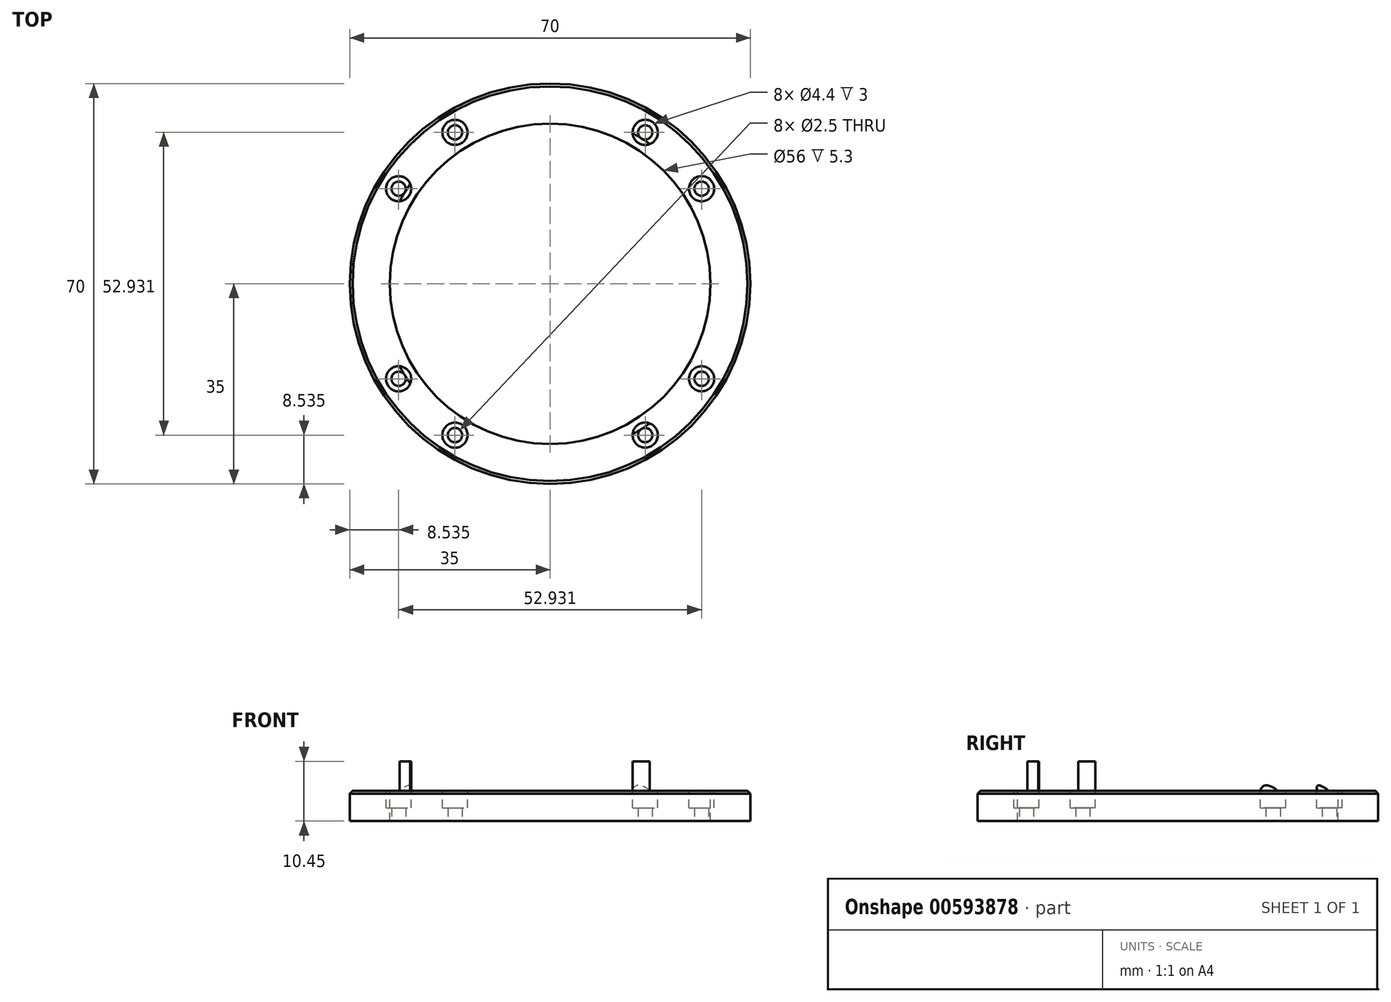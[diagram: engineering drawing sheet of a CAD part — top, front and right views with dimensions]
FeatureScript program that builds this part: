
annotation { "Feature Type Name" : "Feature", "Feature Type Description" : "" }
export const myFeature = defineFeature(function(context is Context, id is Id, definition is map)
    precondition{}
    {
        {
            var Q0;
            Q0=qCreatedBy(makeId("Top.planeOp"),FACE);
            var sketch = newSketch(context, id + "F0", { "sketchPlane" : qUnion([Q0])});
            skCircle(sketch, "E0", {"center": v(0, 0) * mm, "radius": 27 * mm});
            skCircle(sketch, "E1", {"center": v(0, 0) * mm, "radius": 25 * mm});
            skCircle(sketch, "E2", {"center": v(0, 0) * mm, "radius": 34.5 * mm});
            skLineSegment(sketch, "E3", {"start": v(-12.5, 31.4) * mm, "end": v(-12.5, 32.16) * mm});
            skLineSegment(sketch, "E4", {"start": v(-12.5, 32.16) * mm, "end": v(-12.5, 23.93) * mm});
            skLineSegment(sketch, "E5", {"start": v(12.5, 31.4) * mm, "end": v(12.5, 32.16) * mm});
            skLineSegment(sketch, "E6", {"start": v(12.5, 32.16) * mm, "end": v(12.5, 23.93) * mm});
            skLineSegment(sketch, "E7.1.0", {"start": v(-32.16, -12.5) * mm, "end": v(-23.93, -12.5) * mm});
            skLineSegment(sketch, "E7.1.1", {"start": v(-32.16, 12.5) * mm, "end": v(-23.93, 12.5) * mm});
            skLineSegment(sketch, "E7.2.0", {"start": v(12.5, -32.16) * mm, "end": v(12.5, -23.93) * mm});
            skLineSegment(sketch, "E7.2.1", {"start": v(-12.5, -32.16) * mm, "end": v(-12.5, -23.93) * mm});
            skLineSegment(sketch, "E7.3.0", {"start": v(32.16, 12.5) * mm, "end": v(23.93, 12.5) * mm});
            skLineSegment(sketch, "E7.3.1", {"start": v(32.16, -12.5) * mm, "end": v(23.93, -12.5) * mm});
            skCircle(sketch, "E8", {"center": v(0, 0) * mm, "radius": 28.99 * mm});
            skLineSegment(sketch, "E9", {"start": v(12.5, 32.16) * mm, "end": v(12.5, 26.16) * mm});
            skLineSegment(sketch, "E10", {"start": v(-12.5, 32.16) * mm, "end": v(-12.5, 26.16) * mm});
            skLineSegment(sketch, "E11", {"start": v(0, 34.5) * mm, "end": v(0, 30.5) * mm});
            skLineSegment(sketch, "E12", {"start": v(0, 30.5) * mm, "end": v(0, 32) * mm});
            skCircle(sketch, "E13", {"center": v(0, 32) * mm, "radius": 1.5 * mm});
            skLineSegment(sketch, "E14", {"start": v(-1.5, 32) * mm, "end": v(-1.5, 34.47) * mm});
            skLineSegment(sketch, "E15", {"start": v(1.5, 32) * mm, "end": v(1.5, 34.47) * mm});
            skCircle(sketch, "E16.1.0", {"center": v(-32, 0) * mm, "radius": 1.5 * mm});
            skLineSegment(sketch, "E16.1.1", {"start": v(-34.5, 0) * mm, "end": v(-30.5, 0) * mm});
            skLineSegment(sketch, "E16.1.2", {"start": v(-32, -1.5) * mm, "end": v(-34.47, -1.5) * mm});
            skLineSegment(sketch, "E16.1.3", {"start": v(-32, 1.5) * mm, "end": v(-34.47, 1.5) * mm});
            skCircle(sketch, "E16.2.0", {"center": v(0, -32) * mm, "radius": 1.5 * mm});
            skLineSegment(sketch, "E16.2.1", {"start": v(0, -34.5) * mm, "end": v(0, -30.5) * mm});
            skLineSegment(sketch, "E16.2.2", {"start": v(1.5, -32) * mm, "end": v(1.5, -34.47) * mm});
            skLineSegment(sketch, "E16.2.3", {"start": v(-1.5, -32) * mm, "end": v(-1.5, -34.47) * mm});
            skCircle(sketch, "E16.3.0", {"center": v(32, 0) * mm, "radius": 1.5 * mm});
            skLineSegment(sketch, "E16.3.1", {"start": v(34.5, 0) * mm, "end": v(30.5, 0) * mm});
            skLineSegment(sketch, "E16.3.2", {"start": v(32, 1.5) * mm, "end": v(34.47, 1.5) * mm});
            skLineSegment(sketch, "E16.3.3", {"start": v(32, -1.5) * mm, "end": v(34.47, -1.5) * mm});
            skSolve(sketch);
        }
        {
            var Q0;
            {var subQ0=sQuery(id+"F0.wireOp",EDGE,"E7.1.0");Q0=makeQuery(id+"F0.imprint","IMPRINT",FACE,{"disambiguationData":[TD([[makeQuery(id+"F0.imprint","IMPRINT",EDGE,{"derivedFrom":subQ0}),1.0]])]});}
            var Q1;
            {var subQ0=sQuery(id+"F0.wireOp",EDGE,"E7.2.0");Q1=makeQuery(id+"F0.imprint","IMPRINT",FACE,{"disambiguationData":[TD([[makeQuery(id+"F0.imprint","IMPRINT",EDGE,{"derivedFrom":subQ0}),1.0]])]});}
            var Q2;
            {var subQ0=sQuery(id+"F0.wireOp",EDGE,"E7.3.0");Q2=makeQuery(id+"F0.imprint","IMPRINT",FACE,{"disambiguationData":[TD([[makeQuery(id+"F0.imprint","IMPRINT",EDGE,{"derivedFrom":subQ0}),1.0]])]});}
            var Q3;
            {var subQ0=sQuery(id+"F0.wireOp",EDGE,"E4");var subQ3=makeQuery(id+"F0.imprint","IMPRINT",VERTEX,{"derivedFrom":subQ0});Q3=makeQuery(id+"F0.imprint","IMPRINT",FACE,{"disambiguationData":[TD([[makeQuery(id+"F0.imprint","IMPRINT",EDGE,{"disambiguationData":[TD([[subQ3,1.0]])],"derivedFrom":subQ0}),1.0]])]});}
            var Q4;
            {var subQ0=sQuery(id+"F0.wireOp",EDGE,"E4");var subQ1=sQuery(id+"F0.wireOp",EDGE,"E0");var subQ2=makeQuery(id+"F0.imprint","INTERSECT",VERTEX,{"derivedFrom":[subQ1,subQ0]});Q4=makeQuery(id+"F0.imprint","IMPRINT",FACE,{"disambiguationData":[TD([[makeQuery(id+"F0.imprint","IMPRINT",EDGE,{"disambiguationData":[TD([[subQ2,-1.0]])],"derivedFrom":subQ1}),-1.0]])]});}
            var Q5;
            {var subQ0=sQuery(id+"F0.wireOp",EDGE,"E6");var subQ1=sQuery(id+"F0.wireOp",EDGE,"E0");var subQ2=makeQuery(id+"F0.imprint","INTERSECT",VERTEX,{"derivedFrom":[subQ1,subQ0]});Q5=makeQuery(id+"F0.imprint","IMPRINT",FACE,{"disambiguationData":[TD([[makeQuery(id+"F0.imprint","IMPRINT",EDGE,{"disambiguationData":[TD([[subQ2,1.0]])],"derivedFrom":subQ1}),-1.0]])]});}
            var Q6;
            {var subQ0=sQuery(id+"F0.wireOp",EDGE,"E7.2.0");var subQ1=sQuery(id+"F0.wireOp",EDGE,"E0");var subQ2=makeQuery(id+"F0.imprint","INTERSECT",VERTEX,{"derivedFrom":[subQ1,subQ0]});Q6=makeQuery(id+"F0.imprint","IMPRINT",FACE,{"disambiguationData":[TD([[makeQuery(id+"F0.imprint","IMPRINT",EDGE,{"disambiguationData":[TD([[subQ2,-1.0]])],"derivedFrom":subQ1}),-1.0]])]});}
            var Q7;
            {var subQ0=sQuery(id+"F0.wireOp",EDGE,"E7.1.0");var subQ1=sQuery(id+"F0.wireOp",EDGE,"E0");var subQ2=makeQuery(id+"F0.imprint","INTERSECT",VERTEX,{"derivedFrom":[subQ1,subQ0]});Q7=makeQuery(id+"F0.imprint","IMPRINT",FACE,{"disambiguationData":[TD([[makeQuery(id+"F0.imprint","IMPRINT",EDGE,{"disambiguationData":[TD([[subQ2,-1.0]])],"derivedFrom":subQ1}),-1.0]])]});}
            var Q8;
            {var subQ0=sQuery(id+"F0.wireOp",EDGE,"E4");var subQ1=sQuery(id+"F0.wireOp",EDGE,"E0");var subQ2=makeQuery(id+"F0.imprint","INTERSECT",VERTEX,{"derivedFrom":[subQ1,subQ0]});Q8=makeQuery(id+"F0.imprint","IMPRINT",FACE,{"disambiguationData":[TD([[makeQuery(id+"F0.imprint","IMPRINT",EDGE,{"disambiguationData":[TD([[subQ2,1.0]])],"derivedFrom":subQ1}),-1.0]])]});}
            var Q9;
            {var subQ0=sQuery(id+"F0.wireOp",EDGE,"E9");var subQ3=makeQuery(id+"F0.imprint","IMPRINT",VERTEX,{"derivedFrom":subQ0});Q9=makeQuery(id+"F0.imprint","IMPRINT",FACE,{"disambiguationData":[TD([[makeQuery(id+"F0.imprint","IMPRINT",EDGE,{"disambiguationData":[TD([[subQ3,1.0]])],"derivedFrom":subQ0}),-1.0]])]});}
            var Q10;
            {var subQ11=sQuery(id+"F0.wireOp",EDGE,"E16.3.2");Q10=makeQuery(id+"F0.imprint","IMPRINT",FACE,{"disambiguationData":[TD([[makeQuery(id+"F0.imprint","IMPRINT",EDGE,{"derivedFrom":subQ11}),1.0]])]});}
            var Q11;
            {var subQ6=sQuery(id+"F0.wireOp",EDGE,"E16.2.2");Q11=makeQuery(id+"F0.imprint","IMPRINT",FACE,{"disambiguationData":[TD([[makeQuery(id+"F0.imprint","IMPRINT",EDGE,{"derivedFrom":subQ6}),1.0]])]});}
            var Q12;
            {var subQ7=sQuery(id+"F0.wireOp",EDGE,"E16.1.2");Q12=makeQuery(id+"F0.imprint","IMPRINT",FACE,{"disambiguationData":[TD([[makeQuery(id+"F0.imprint","IMPRINT",EDGE,{"derivedFrom":subQ7}),1.0]])]});}
            extrude(context, id + "F1", {"entities" : qUnion([Q0, Q1, Q2, Q3, Q4, Q5, Q6, Q7, Q8, Q9, Q10, Q11, Q12]), "depth" : 2 * mm, "offsetDistance" : 25 * mm});
        }
        {
            var Q0;
            Q0=qCreatedBy(makeId("Top.planeOp"),FACE);
            var sketch = newSketch(context, id + "F2", { "sketchPlane" : qUnion([Q0])});
            skCircle(sketch, "E17", {"center": v(0, 0) * mm, "radius": 27.1 * mm});
            skCircle(sketch, "E18", {"center": v(0, 0) * mm, "radius": 24.55 * mm});
            skSolve(sketch);
        }
        {
            var Q0;
            Q0=makeQuery(id+"F2.imprint","IMPRINT",FACE,{"disambiguationData":[TD([[makeQuery(id+"F2.imprint","IMPRINT",EDGE,{"derivedFrom":sQuery(id+"F2.wireOp",EDGE,"E17")}),1.0]])]});
            extrude(context, id + "F3", {"entities" : qUnion([Q0]), "operationType" : NewBodyOperationType.ADD, "depth" : 10 * mm, "offsetDistance" : 25 * mm});
        }
        {
            var Q0;
            Q0=qCreatedBy(makeId("Top.planeOp"),FACE);
            var sketch = newSketch(context, id + "F4", { "sketchPlane" : qUnion([Q0])});
            skCircle(sketch, "E19", {"center": v(0, 0) * mm, "radius": 28 * mm});
            skCircle(sketch, "E20", {"center": v(0, 0) * mm, "radius": 30 * mm});
            skSolve(sketch);
        }
        {
            var Q0;
            Q0=makeQuery(id+"F4.imprint","IMPRINT",FACE,{"disambiguationData":[TD([[makeQuery(id+"F4.imprint","IMPRINT",EDGE,{"derivedFrom":sQuery(id+"F4.wireOp",EDGE,"E19")}),-1.0]])]});
            extrude(context, id + "F5", {"entities" : qUnion([Q0]), "operationType" : NewBodyOperationType.ADD, "oppositeDirection" : true, "depth" : 5.15 * mm, "offsetDistance" : 25 * mm});
        }
        {
            var Q0;
            Q0=makeQuery(id+"F5.opExtrude","CAP_FACE",FACE,{"disambiguationData":[OSD([sQuery(id+"F4.wireOp",EDGE,"E19"),sQuery(id+"F4.wireOp",EDGE,"E20")])],"isStart":false});
            var sketch = newSketch(context, id + "F6", { "sketchPlane" : qUnion([Q0])});
            skCircle(sketch, "E21", {"center": v(0, 0) * mm, "radius": 35 * mm});
            skCircle(sketch, "E22", {"center": v(0, 0) * mm, "radius": 28 * mm});
            skLineSegment(sketch, "E23", {"start": v(0, 0) * mm, "end": v(-35, 0) * mm});
            skLineSegment(sketch, "E24", {"start": v(0, 0) * mm, "end": v(0, 35) * mm});
            skLineSegment(sketch, "E25", {"start": v(0, 0) * mm, "end": v(35, 0) * mm});
            skCircle(sketch, "E26", {"center": v(-26.47, 16.62) * mm, "radius": 1.25 * mm});
            skCircle(sketch, "E27", {"center": v(-26.47, 16.62) * mm, "radius": 2.2 * mm});
            skCircle(sketch, "E28", {"center": v(-16.62, 26.47) * mm, "radius": 1.25 * mm});
            skCircle(sketch, "E29", {"center": v(-16.62, 26.47) * mm, "radius": 2.2 * mm});
            skCircle(sketch, "E30.1.0", {"center": v(-16.62, -26.47) * mm, "radius": 2.2 * mm});
            skCircle(sketch, "E30.1.1", {"center": v(-16.62, -26.47) * mm, "radius": 1.25 * mm});
            skCircle(sketch, "E30.1.2", {"center": v(-26.47, -16.62) * mm, "radius": 2.2 * mm});
            skCircle(sketch, "E30.1.3", {"center": v(-26.47, -16.62) * mm, "radius": 1.25 * mm});
            skCircle(sketch, "E30.2.0", {"center": v(26.47, -16.62) * mm, "radius": 2.2 * mm});
            skCircle(sketch, "E30.2.1", {"center": v(26.47, -16.62) * mm, "radius": 1.25 * mm});
            skCircle(sketch, "E30.2.2", {"center": v(16.62, -26.47) * mm, "radius": 2.2 * mm});
            skCircle(sketch, "E30.2.3", {"center": v(16.62, -26.47) * mm, "radius": 1.25 * mm});
            skCircle(sketch, "E31.1.3.0", {"center": v(16.62, 26.47) * mm, "radius": 2.2 * mm});
            skCircle(sketch, "E31.2.3.0", {"center": v(16.62, 26.47) * mm, "radius": 1.25 * mm});
            skCircle(sketch, "E31.4.3.0", {"center": v(26.47, 16.62) * mm, "radius": 2.2 * mm});
            skCircle(sketch, "E31.6.3.0", {"center": v(26.47, 16.62) * mm, "radius": 1.25 * mm});
            skLineSegment(sketch, "E32", {"start": v(-15.95, 25.4) * mm, "end": v(15.95, -25.4) * mm});
            skSolve(sketch);
        }
        {
            var Q0;
            Q0 = qSketchRegion(id + "F6", true);
            extrude(context, id + "F7", {"entities" : qUnion([Q0]), "operationType" : NewBodyOperationType.ADD, "depth" : 5.3 * mm, "offsetDistance" : 25 * mm});
        }
        {
            var Q0;
            Q0=makeQuery(id+"F7.opExtrude","CAP_EDGE",EDGE,{"disambiguationData":[OSD([sQuery(id+"F6.wireOp",EDGE,"E21")])],"isStart":true});
            chamfer(context, id + "F8", {"entities" : qUnion([Q0]), "width" : 0.5 * mm, "tangentPropagation" : true});
        }
        {
            var Q0;
            {var subQ0=sQuery(id+"F0.wireOp",EDGE,"E2");Q0=makeQuery(id+"F1.opExtrude","CAP_EDGE",EDGE,{"disambiguationData":[OSD([subQ0]),TDD([makeQuery(id+"F0.imprint","IMPRINT",EDGE,{"disambiguationData":[TD([[makeQuery(id+"F0.imprint","INTERSECT",VERTEX,{"derivedFrom":[subQ0,sQuery(id+"F0.wireOp",EDGE,"E7.2.0")]}),1.0]])],"derivedFrom":subQ0})])],"isStart":false});}
            var Q1;
            {var subQ0=sQuery(id+"F0.wireOp",EDGE,"E2");Q1=makeQuery(id+"F1.opExtrude","CAP_EDGE",EDGE,{"disambiguationData":[OSD([subQ0]),TDD([makeQuery(id+"F0.imprint","IMPRINT",EDGE,{"disambiguationData":[TD([[makeQuery(id+"F0.imprint","INTERSECT",VERTEX,{"derivedFrom":[subQ0,sQuery(id+"F0.wireOp",EDGE,"E7.3.0")]}),1.0]])],"derivedFrom":subQ0})])],"isStart":false});}
            var Q2;
            {var subQ0=sQuery(id+"F0.wireOp",EDGE,"E2");Q2=makeQuery(id+"F1.opExtrude","CAP_EDGE",EDGE,{"disambiguationData":[OSD([subQ0]),TDD([makeQuery(id+"F0.imprint","IMPRINT",EDGE,{"disambiguationData":[TD([[makeQuery(id+"F0.imprint","INTERSECT",VERTEX,{"derivedFrom":[subQ0,sQuery(id+"F0.wireOp",EDGE,"E7.1.0")]}),1.0]])],"derivedFrom":subQ0})])],"isStart":false});}
            var Q3;
            {var subQ0=sQuery(id+"F0.wireOp",EDGE,"E2");Q3=makeQuery(id+"F1.opExtrude","CAP_EDGE",EDGE,{"disambiguationData":[OSD([subQ0]),TDD([makeQuery(id+"F0.imprint","IMPRINT",EDGE,{"disambiguationData":[TD([[makeQuery(id+"F0.imprint","INTERSECT",VERTEX,{"derivedFrom":[subQ0,sQuery(id+"F0.wireOp",EDGE,"E9")]}),-1.0]])],"derivedFrom":subQ0})])],"isStart":false});}
            var Q4;
            Q4=makeQuery(id+"F3.opExtrude","CAP_EDGE",EDGE,{"disambiguationData":[OSD([sQuery(id+"F2.wireOp",EDGE,"E17")])],"isStart":false});
            var Q5;
            {var subQ0=sQuery(id+"F0.wireOp",EDGE,"E2");Q5=makeQuery(id+"F1.opExtrude","CAP_EDGE",EDGE,{"disambiguationData":[OSD([subQ0]),TDD([makeQuery(id+"F0.imprint","IMPRINT",EDGE,{"disambiguationData":[TD([[makeQuery(id+"F0.imprint","INTERSECT",VERTEX,{"derivedFrom":[subQ0,sQuery(id+"F0.wireOp",EDGE,"E10")]}),1.0]])],"derivedFrom":subQ0})])],"isStart":false});}
            var Q6;
            {var subQ0=sQuery(id+"F0.wireOp",EDGE,"E2");Q6=makeQuery(id+"F1.opExtrude","CAP_EDGE",EDGE,{"disambiguationData":[OSD([subQ0]),TDD([makeQuery(id+"F0.imprint","IMPRINT",EDGE,{"disambiguationData":[TD([[makeQuery(id+"F0.imprint","INTERSECT",VERTEX,{"derivedFrom":[subQ0,sQuery(id+"F0.wireOp",EDGE,"E7.1.1")]}),-1.0]])],"derivedFrom":subQ0})])],"isStart":false});}
            var Q7;
            {var subQ0=sQuery(id+"F0.wireOp",EDGE,"E2");Q7=makeQuery(id+"F1.opExtrude","CAP_EDGE",EDGE,{"disambiguationData":[OSD([subQ0]),TDD([makeQuery(id+"F0.imprint","IMPRINT",EDGE,{"disambiguationData":[TD([[makeQuery(id+"F0.imprint","INTERSECT",VERTEX,{"derivedFrom":[subQ0,sQuery(id+"F0.wireOp",EDGE,"E7.2.1")]}),-1.0]])],"derivedFrom":subQ0})])],"isStart":false});}
            var Q8;
            {var subQ0=sQuery(id+"F0.wireOp",EDGE,"E2");Q8=makeQuery(id+"F1.opExtrude","CAP_EDGE",EDGE,{"disambiguationData":[OSD([subQ0]),TDD([makeQuery(id+"F0.imprint","IMPRINT",EDGE,{"disambiguationData":[TD([[makeQuery(id+"F0.imprint","INTERSECT",VERTEX,{"derivedFrom":[subQ0,sQuery(id+"F0.wireOp",EDGE,"E7.3.1")]}),-1.0]])],"derivedFrom":subQ0})])],"isStart":false});}
            var Q9;
            Q9=makeQuery(id+"F1.opExtrude","SWEPT_EDGE",EDGE,{"disambiguationData":[OSD([sQuery(id+"F0.wireOp",EDGE,"E2"),sQuery(id+"F0.wireOp",EDGE,"E10")])]});
            var Q10;
            {var subQ0=sQuery(id+"F0.wireOp",EDGE,"E2");Q10=makeQuery(id+"F1.opExtrude","CAP_EDGE",EDGE,{"disambiguationData":[OSD([subQ0]),TDD([makeQuery(id+"F0.imprint","IMPRINT",EDGE,{"disambiguationData":[TD([[makeQuery(id+"F0.imprint","INTERSECT",VERTEX,{"derivedFrom":[subQ0,sQuery(id+"F0.wireOp",EDGE,"E10")]}),1.0]])],"derivedFrom":subQ0})])],"isStart":true});}
            var Q11;
            {var subQ0=sQuery(id+"F0.wireOp",EDGE,"E2");Q11=makeQuery(id+"F1.opExtrude","CAP_EDGE",EDGE,{"disambiguationData":[OSD([subQ0]),TDD([makeQuery(id+"F0.imprint","IMPRINT",EDGE,{"disambiguationData":[TD([[makeQuery(id+"F0.imprint","INTERSECT",VERTEX,{"derivedFrom":[subQ0,sQuery(id+"F0.wireOp",EDGE,"E9")]}),-1.0]])],"derivedFrom":subQ0})])],"isStart":true});}
            var Q12;
            Q12=makeQuery(id+"F1.opExtrude","SWEPT_EDGE",EDGE,{"disambiguationData":[OSD([sQuery(id+"F0.wireOp",EDGE,"E2"),sQuery(id+"F0.wireOp",EDGE,"E9")])]});
            var Q13;
            Q13=makeQuery(id+"F1.opExtrude","SWEPT_EDGE",EDGE,{"disambiguationData":[OSD([sQuery(id+"F0.wireOp",EDGE,"E2"),sQuery(id+"F0.wireOp",EDGE,"E7.2.1")])]});
            var Q14;
            Q14=makeQuery(id+"F1.opExtrude","SWEPT_EDGE",EDGE,{"disambiguationData":[OSD([sQuery(id+"F0.wireOp",EDGE,"E2"),sQuery(id+"F0.wireOp",EDGE,"E7.1.0")])]});
            var Q15;
            Q15=makeQuery(id+"F1.opExtrude","SWEPT_EDGE",EDGE,{"disambiguationData":[OSD([sQuery(id+"F0.wireOp",EDGE,"E2"),sQuery(id+"F0.wireOp",EDGE,"E16.1.2")])]});
            var Q16;
            Q16=makeQuery(id+"F1.opExtrude","SWEPT_EDGE",EDGE,{"disambiguationData":[OSD([sQuery(id+"F0.wireOp",EDGE,"E2"),sQuery(id+"F0.wireOp",EDGE,"E7.1.1")])]});
            var Q17;
            {var subQ0=sQuery(id+"F0.wireOp",EDGE,"E2");Q17=makeQuery(id+"F1.opExtrude","CAP_EDGE",EDGE,{"disambiguationData":[OSD([subQ0]),TDD([makeQuery(id+"F0.imprint","IMPRINT",EDGE,{"disambiguationData":[TD([[makeQuery(id+"F0.imprint","INTERSECT",VERTEX,{"derivedFrom":[subQ0,sQuery(id+"F0.wireOp",EDGE,"E7.1.1")]}),-1.0]])],"derivedFrom":subQ0})])],"isStart":true});}
            var Q18;
            {var subQ0=sQuery(id+"F0.wireOp",EDGE,"E2");Q18=makeQuery(id+"F1.opExtrude","CAP_EDGE",EDGE,{"disambiguationData":[OSD([subQ0]),TDD([makeQuery(id+"F0.imprint","IMPRINT",EDGE,{"disambiguationData":[TD([[makeQuery(id+"F0.imprint","INTERSECT",VERTEX,{"derivedFrom":[subQ0,sQuery(id+"F0.wireOp",EDGE,"E7.1.0")]}),1.0]])],"derivedFrom":subQ0})])],"isStart":true});}
            var Q19;
            {var subQ0=sQuery(id+"F0.wireOp",EDGE,"E2");Q19=makeQuery(id+"F1.opExtrude","CAP_EDGE",EDGE,{"disambiguationData":[OSD([subQ0]),TDD([makeQuery(id+"F0.imprint","IMPRINT",EDGE,{"disambiguationData":[TD([[makeQuery(id+"F0.imprint","INTERSECT",VERTEX,{"derivedFrom":[subQ0,sQuery(id+"F0.wireOp",EDGE,"E7.2.1")]}),-1.0]])],"derivedFrom":subQ0})])],"isStart":true});}
            var Q20;
            {var subQ0=sQuery(id+"F0.wireOp",EDGE,"E2");Q20=makeQuery(id+"F1.opExtrude","CAP_EDGE",EDGE,{"disambiguationData":[OSD([subQ0]),TDD([makeQuery(id+"F0.imprint","IMPRINT",EDGE,{"disambiguationData":[TD([[makeQuery(id+"F0.imprint","INTERSECT",VERTEX,{"derivedFrom":[subQ0,sQuery(id+"F0.wireOp",EDGE,"E7.2.0")]}),1.0]])],"derivedFrom":subQ0})])],"isStart":true});}
            var Q21;
            Q21=makeQuery(id+"F1.opExtrude","SWEPT_EDGE",EDGE,{"disambiguationData":[OSD([sQuery(id+"F0.wireOp",EDGE,"E2"),sQuery(id+"F0.wireOp",EDGE,"E7.2.0")])]});
            var Q22;
            {var subQ0=sQuery(id+"F0.wireOp",EDGE,"E2");Q22=makeQuery(id+"F1.opExtrude","CAP_EDGE",EDGE,{"disambiguationData":[OSD([subQ0]),TDD([makeQuery(id+"F0.imprint","IMPRINT",EDGE,{"disambiguationData":[TD([[makeQuery(id+"F0.imprint","INTERSECT",VERTEX,{"derivedFrom":[subQ0,sQuery(id+"F0.wireOp",EDGE,"E7.3.1")]}),-1.0]])],"derivedFrom":subQ0})])],"isStart":true});}
            var Q23;
            Q23=makeQuery(id+"F1.opExtrude","SWEPT_EDGE",EDGE,{"disambiguationData":[OSD([sQuery(id+"F0.wireOp",EDGE,"E2"),sQuery(id+"F0.wireOp",EDGE,"E7.3.1")])]});
            var Q24;
            {var subQ0=sQuery(id+"F0.wireOp",EDGE,"E2");Q24=makeQuery(id+"F1.opExtrude","CAP_EDGE",EDGE,{"disambiguationData":[OSD([subQ0]),TDD([makeQuery(id+"F0.imprint","IMPRINT",EDGE,{"disambiguationData":[TD([[makeQuery(id+"F0.imprint","INTERSECT",VERTEX,{"derivedFrom":[subQ0,sQuery(id+"F0.wireOp",EDGE,"E7.3.0")]}),1.0]])],"derivedFrom":subQ0})])],"isStart":true});}
            var Q25;
            Q25=makeQuery(id+"F1.opExtrude","SWEPT_EDGE",EDGE,{"disambiguationData":[OSD([sQuery(id+"F0.wireOp",EDGE,"E2"),sQuery(id+"F0.wireOp",EDGE,"E7.3.0")])]});
            chamfer(context, id + "F9", {"entities" : qUnion([Q0, Q1, Q2, Q3, Q4, Q5, Q6, Q7, Q8, Q9, Q10, Q11, Q12, Q13, Q14, Q15, Q16, Q17, Q18, Q19, Q20, Q21, Q22, Q23, Q24, Q25]), "width" : 0.5 * mm, "tangentPropagation" : true});
        }
        {
            var Q0;
            Q0=makeQuery(id+"F1.opExtrude","SWEPT_EDGE",EDGE,{"disambiguationData":[OSD([sQuery(id+"F0.wireOp",EDGE,"E7.2.0"),sQuery(id+"F0.wireOp",EDGE,"E8")])]});
            var Q1;
            Q1=makeQuery(id+"F1.opExtrude","SWEPT_EDGE",EDGE,{"disambiguationData":[OSD([sQuery(id+"F0.wireOp",EDGE,"E7.3.1"),sQuery(id+"F0.wireOp",EDGE,"E8")])]});
            var Q2;
            Q2=makeQuery(id+"F1.opExtrude","SWEPT_EDGE",EDGE,{"disambiguationData":[OSD([sQuery(id+"F0.wireOp",EDGE,"E7.3.0"),sQuery(id+"F0.wireOp",EDGE,"E8")])]});
            var Q3;
            Q3=makeQuery(id+"F1.opExtrude","SWEPT_EDGE",EDGE,{"disambiguationData":[OSD([sQuery(id+"F0.wireOp",EDGE,"E6"),sQuery(id+"F0.wireOp",EDGE,"E8"),sQuery(id+"F0.wireOp",EDGE,"E9")])]});
            var Q4;
            Q4=makeQuery(id+"F1.opExtrude","SWEPT_EDGE",EDGE,{"disambiguationData":[OSD([sQuery(id+"F0.wireOp",EDGE,"E7.2.1"),sQuery(id+"F0.wireOp",EDGE,"E8")])]});
            var Q5;
            Q5=makeQuery(id+"F1.opExtrude","SWEPT_EDGE",EDGE,{"disambiguationData":[OSD([sQuery(id+"F0.wireOp",EDGE,"E7.1.0"),sQuery(id+"F0.wireOp",EDGE,"E8")])]});
            var Q6;
            Q6=makeQuery(id+"F1.opExtrude","SWEPT_EDGE",EDGE,{"disambiguationData":[OSD([sQuery(id+"F0.wireOp",EDGE,"E4"),sQuery(id+"F0.wireOp",EDGE,"E8"),sQuery(id+"F0.wireOp",EDGE,"E10")])]});
            var Q7;
            Q7=makeQuery(id+"F1.opExtrude","SWEPT_EDGE",EDGE,{"disambiguationData":[OSD([sQuery(id+"F0.wireOp",EDGE,"E7.1.1"),sQuery(id+"F0.wireOp",EDGE,"E8")])]});
            fillet(context, id + "F10", {"entities" : qUnion([Q0, Q1, Q2, Q3, Q4, Q5, Q6, Q7]), "radius" : 2.5 * mm, "tangentPropagation" : true, "allowEdgeOverflow" : false});
        }
        {
            var Q0;
            Q0=makeQuery(id+"F3.opExtrude","CAP_EDGE",EDGE,{"disambiguationData":[OSD([sQuery(id+"F2.wireOp",EDGE,"E18")])],"isStart":true});
            fillet(context, id + "F11", {"entities" : qUnion([Q0]), "radius" : 2.5 * mm, "tangentPropagation" : true, "allowEdgeOverflow" : false});
        }
        {
            var Q0;
            Q0=makeQuery(id+"F7.opExtrude","CAP_FACE",FACE,{"disambiguationData":[OSD([sQuery(id+"F6.wireOp",EDGE,"E21"),sQuery(id+"F6.wireOp",EDGE,"E22"),sQuery(id+"F6.wireOp",EDGE,"E27"),sQuery(id+"F6.wireOp",EDGE,"E29"),sQuery(id+"F6.wireOp",EDGE,"E30.1.0"),sQuery(id+"F6.wireOp",EDGE,"E30.1.2"),sQuery(id+"F6.wireOp",EDGE,"E30.2.0"),sQuery(id+"F6.wireOp",EDGE,"E30.2.2"),sQuery(id+"F6.wireOp",EDGE,"E31.1.3.0"),sQuery(id+"F6.wireOp",EDGE,"E31.4.3.0")])],"isStart":false});
            var sketch = newSketch(context, id + "F12", { "sketchPlane" : qUnion([Q0])});
            skCircle(sketch, "E33", {"center": v(16.62, 26.47) * mm, "radius": 2.2 * mm});
            skPoint(sketch, "E33.first.point", {"position": v(16.62, 28.67) * mm});
            skPoint(sketch, "E33.second.point", {"position": v(16.62, 24.27) * mm});
            skPoint(sketch, "E33.third.point", {"position": v(18.7, 27.17) * mm});
            skCircle(sketch, "E34", {"center": v(26.47, 16.62) * mm, "radius": 2.2 * mm});
            skPoint(sketch, "E34.first.point", {"position": v(26.47, 18.82) * mm});
            skPoint(sketch, "E34.second.point", {"position": v(26.47, 14.42) * mm});
            skPoint(sketch, "E34.third.point", {"position": v(28.44, 17.6) * mm});
            skCircle(sketch, "E35", {"center": v(16.62, 26.47) * mm, "radius": 1.25 * mm});
            skCircle(sketch, "E36", {"center": v(26.47, 16.62) * mm, "radius": 1.25 * mm});
            skCircle(sketch, "E37.1.0", {"center": v(-26.47, 16.62) * mm, "radius": 1.25 * mm});
            skCircle(sketch, "E37.1.1", {"center": v(-26.47, 16.62) * mm, "radius": 2.2 * mm});
            skCircle(sketch, "E37.1.2", {"center": v(-16.62, 26.47) * mm, "radius": 1.25 * mm});
            skCircle(sketch, "E37.1.3", {"center": v(-16.62, 26.47) * mm, "radius": 2.2 * mm});
            skCircle(sketch, "E37.2.0", {"center": v(-16.62, -26.47) * mm, "radius": 1.25 * mm});
            skCircle(sketch, "E37.2.1", {"center": v(-16.62, -26.47) * mm, "radius": 2.2 * mm});
            skCircle(sketch, "E37.2.2", {"center": v(-26.47, -16.62) * mm, "radius": 1.25 * mm});
            skCircle(sketch, "E37.2.3", {"center": v(-26.47, -16.62) * mm, "radius": 2.2 * mm});
            skCircle(sketch, "E37.3.0", {"center": v(26.47, -16.62) * mm, "radius": 1.25 * mm});
            skCircle(sketch, "E37.3.1", {"center": v(26.47, -16.62) * mm, "radius": 2.2 * mm});
            skCircle(sketch, "E37.3.2", {"center": v(16.62, -26.47) * mm, "radius": 1.25 * mm});
            skCircle(sketch, "E37.3.3", {"center": v(16.62, -26.47) * mm, "radius": 2.2 * mm});
            skPoint(sketch, "E37.center", {"position": v(0, 0) * mm});
            skSolve(sketch);
        }
        {
            var Q0;
            Q0=makeQuery(id+"F12.imprint","IMPRINT",FACE,{"disambiguationData":[TD([[makeQuery(id+"F12.imprint","IMPRINT",EDGE,{"derivedFrom":sQuery(id+"F12.wireOp",EDGE,"E37.1.2")}),-1.0]])]});
            var Q1;
            Q1=makeQuery(id+"F12.imprint","IMPRINT",FACE,{"disambiguationData":[TD([[makeQuery(id+"F12.imprint","IMPRINT",EDGE,{"derivedFrom":sQuery(id+"F12.wireOp",EDGE,"E37.1.0")}),-1.0]])]});
            var Q2;
            Q2=makeQuery(id+"F12.imprint","IMPRINT",FACE,{"disambiguationData":[TD([[makeQuery(id+"F12.imprint","IMPRINT",EDGE,{"derivedFrom":sQuery(id+"F12.wireOp",EDGE,"E33")}),1.0]])]});
            var Q3;
            Q3=makeQuery(id+"F12.imprint","IMPRINT",FACE,{"disambiguationData":[TD([[makeQuery(id+"F12.imprint","IMPRINT",EDGE,{"derivedFrom":sQuery(id+"F12.wireOp",EDGE,"E34")}),1.0]])]});
            var Q4;
            Q4=makeQuery(id+"F12.imprint","IMPRINT",FACE,{"disambiguationData":[TD([[makeQuery(id+"F12.imprint","IMPRINT",EDGE,{"derivedFrom":sQuery(id+"F12.wireOp",EDGE,"E37.3.0")}),-1.0]])]});
            var Q5;
            Q5=makeQuery(id+"F12.imprint","IMPRINT",FACE,{"disambiguationData":[TD([[makeQuery(id+"F12.imprint","IMPRINT",EDGE,{"derivedFrom":sQuery(id+"F12.wireOp",EDGE,"E37.2.0")}),-1.0]])]});
            var Q6;
            Q6=makeQuery(id+"F12.imprint","IMPRINT",FACE,{"disambiguationData":[TD([[makeQuery(id+"F12.imprint","IMPRINT",EDGE,{"derivedFrom":sQuery(id+"F12.wireOp",EDGE,"E37.2.2")}),-1.0]])]});
            var Q7;
            Q7=makeQuery(id+"F12.imprint","IMPRINT",FACE,{"disambiguationData":[TD([[makeQuery(id+"F12.imprint","IMPRINT",EDGE,{"derivedFrom":sQuery(id+"F12.wireOp",EDGE,"E37.3.2")}),-1.0]])]});
            extrude(context, id + "F13", {"entities" : qUnion([Q0, Q1, Q2, Q3, Q4, Q5, Q6, Q7]), "operationType" : NewBodyOperationType.ADD, "oppositeDirection" : true, "depth" : 2.3 * mm, "offsetDistance" : 25 * mm});
        }
        {
            var Q0;
            Q0=makeQuery(id+"F7.opExtrude","CAP_FACE",FACE,{"disambiguationData":[OSD([sQuery(id+"F6.wireOp",EDGE,"E21"),sQuery(id+"F6.wireOp",EDGE,"E22"),sQuery(id+"F6.wireOp",EDGE,"E27"),sQuery(id+"F6.wireOp",EDGE,"E29"),sQuery(id+"F6.wireOp",EDGE,"E30.1.0"),sQuery(id+"F6.wireOp",EDGE,"E30.1.2"),sQuery(id+"F6.wireOp",EDGE,"E30.2.0"),sQuery(id+"F6.wireOp",EDGE,"E30.2.2"),sQuery(id+"F6.wireOp",EDGE,"E31.1.3.0"),sQuery(id+"F6.wireOp",EDGE,"E31.4.3.0")])],"isStart":true});
            var sketch = newSketch(context, id + "F14", { "sketchPlane" : qUnion([Q0])});
            skCircle(sketch, "E38", {"center": v(26.47, 16.62) * mm, "radius": 2.2 * mm});
            skPoint(sketch, "E38.first.point", {"position": v(28.16, 15.21) * mm});
            skPoint(sketch, "E38.second.point", {"position": v(24.7, 17.94) * mm});
            skPoint(sketch, "E38.third.point", {"position": v(28.26, 17.88) * mm});
            skCircle(sketch, "E39", {"center": v(16.62, 26.47) * mm, "radius": 2.2 * mm});
            skPoint(sketch, "E39.first.point", {"position": v(18.64, 25.6) * mm});
            skPoint(sketch, "E39.second.point", {"position": v(14.6, 27.32) * mm});
            skPoint(sketch, "E39.third.point", {"position": v(17.79, 28.33) * mm});
            skCircle(sketch, "E40", {"center": v(0, 0) * mm, "radius": 30 * mm});
            skCircle(sketch, "E41.1.0", {"center": v(-26.47, 16.62) * mm, "radius": 2.2 * mm});
            skCircle(sketch, "E41.1.1", {"center": v(-16.62, 26.47) * mm, "radius": 2.2 * mm});
            skCircle(sketch, "E41.2.0", {"center": v(-16.62, -26.47) * mm, "radius": 2.2 * mm});
            skCircle(sketch, "E41.2.1", {"center": v(-26.47, -16.62) * mm, "radius": 2.2 * mm});
            skCircle(sketch, "E41.3.0", {"center": v(26.47, -16.62) * mm, "radius": 2.2 * mm});
            skCircle(sketch, "E41.3.1", {"center": v(16.62, -26.47) * mm, "radius": 2.2 * mm});
            skPoint(sketch, "E42", {"position": v(17.43, 24.42) * mm});
            skPoint(sketch, "E43", {"position": v(14.42, 26.3) * mm});
            skSolve(sketch);
        }
        {
            var Q0;
            {var subQ0=sQuery(id+"F14.wireOp",EDGE,"E38");Q0=makeQuery(id+"F14.imprint","IMPRINT",FACE,{"disambiguationData":[TD([[makeQuery(id+"F14.imprint","IMPRINT",EDGE,{"disambiguationData":[OD(1.0)],"derivedFrom":subQ0}),1.0]])]});}
            var Q1;
            {var subQ0=sQuery(id+"F14.wireOp",EDGE,"E39");Q1=makeQuery(id+"F14.imprint","IMPRINT",FACE,{"disambiguationData":[TD([[makeQuery(id+"F14.imprint","IMPRINT",EDGE,{"disambiguationData":[OD(0.0)],"derivedFrom":subQ0}),1.0]])]});}
            var Q2;
            {var subQ0=sQuery(id+"F14.wireOp",EDGE,"E41.1.1");Q2=makeQuery(id+"F14.imprint","IMPRINT",FACE,{"disambiguationData":[TD([[makeQuery(id+"F14.imprint","IMPRINT",EDGE,{"disambiguationData":[OD(0.0)],"derivedFrom":subQ0}),-1.0]])]});}
            var Q3;
            {var subQ0=sQuery(id+"F14.wireOp",EDGE,"E41.1.1");Q3=makeQuery(id+"F14.imprint","IMPRINT",FACE,{"disambiguationData":[TD([[makeQuery(id+"F14.imprint","IMPRINT",EDGE,{"disambiguationData":[OD(1.0)],"derivedFrom":subQ0}),1.0]])]});}
            var Q4;
            {var subQ0=sQuery(id+"F14.wireOp",EDGE,"E41.1.0");Q4=makeQuery(id+"F14.imprint","IMPRINT",FACE,{"disambiguationData":[TD([[makeQuery(id+"F14.imprint","IMPRINT",EDGE,{"disambiguationData":[OD(0.0)],"derivedFrom":subQ0}),1.0]])]});}
            var Q5;
            {var subQ0=sQuery(id+"F14.wireOp",EDGE,"E41.1.0");Q5=makeQuery(id+"F14.imprint","IMPRINT",FACE,{"disambiguationData":[TD([[makeQuery(id+"F14.imprint","IMPRINT",EDGE,{"disambiguationData":[OD(1.0)],"derivedFrom":subQ0}),-1.0]])]});}
            var Q6;
            {var subQ0=sQuery(id+"F14.wireOp",EDGE,"E41.2.1");Q6=makeQuery(id+"F14.imprint","IMPRINT",FACE,{"disambiguationData":[TD([[makeQuery(id+"F14.imprint","IMPRINT",EDGE,{"disambiguationData":[OD(0.0)],"derivedFrom":subQ0}),-1.0]])]});}
            var Q7;
            {var subQ0=sQuery(id+"F14.wireOp",EDGE,"E41.2.1");Q7=makeQuery(id+"F14.imprint","IMPRINT",FACE,{"disambiguationData":[TD([[makeQuery(id+"F14.imprint","IMPRINT",EDGE,{"disambiguationData":[OD(1.0)],"derivedFrom":subQ0}),1.0]])]});}
            var Q8;
            {var subQ0=sQuery(id+"F14.wireOp",EDGE,"E41.2.0");Q8=makeQuery(id+"F14.imprint","IMPRINT",FACE,{"disambiguationData":[TD([[makeQuery(id+"F14.imprint","IMPRINT",EDGE,{"disambiguationData":[OD(0.0)],"derivedFrom":subQ0}),1.0]])]});}
            var Q9;
            {var subQ0=sQuery(id+"F14.wireOp",EDGE,"E41.2.0");Q9=makeQuery(id+"F14.imprint","IMPRINT",FACE,{"disambiguationData":[TD([[makeQuery(id+"F14.imprint","IMPRINT",EDGE,{"disambiguationData":[OD(1.0)],"derivedFrom":subQ0}),-1.0]])]});}
            var Q10;
            {var subQ0=sQuery(id+"F14.wireOp",EDGE,"E41.3.1");Q10=makeQuery(id+"F14.imprint","IMPRINT",FACE,{"disambiguationData":[TD([[makeQuery(id+"F14.imprint","IMPRINT",EDGE,{"disambiguationData":[OD(0.0)],"derivedFrom":subQ0}),-1.0]])]});}
            var Q11;
            {var subQ0=sQuery(id+"F14.wireOp",EDGE,"E41.3.1");Q11=makeQuery(id+"F14.imprint","IMPRINT",FACE,{"disambiguationData":[TD([[makeQuery(id+"F14.imprint","IMPRINT",EDGE,{"disambiguationData":[OD(1.0)],"derivedFrom":subQ0}),1.0]])]});}
            var Q12;
            {var subQ0=sQuery(id+"F14.wireOp",EDGE,"E41.3.0");Q12=makeQuery(id+"F14.imprint","IMPRINT",FACE,{"disambiguationData":[TD([[makeQuery(id+"F14.imprint","IMPRINT",EDGE,{"disambiguationData":[OD(0.0)],"derivedFrom":subQ0}),1.0]])]});}
            extrude(context, id + "F15", {"entities" : qUnion([Q0, Q1, Q2, Q3, Q4, Q5, Q6, Q7, Q8, Q9, Q10, Q11, Q12]), "operationType" : NewBodyOperationType.REMOVE, "endBound" : BoundingType.THROUGH_ALL, "depth" : 6.1 * mm, "offsetDistance" : 25 * mm});
        }
        {
            var Q0;
            {var subQ0=sQuery(id+"F4.wireOp",EDGE,"E20");var subQ1=makeQuery(id+"F5.opExtrude","SWEPT_FACE",FACE,{"disambiguationData":[OSD([subQ0])]});var subQ2=makeQuery(id+"F5.opExtrude","CAP_FACE",FACE,{"disambiguationData":[OSD([sQuery(id+"F4.wireOp",EDGE,"E19"),subQ0])],"isStart":true});var subQ3=sQuery(id+"F0.wireOp",EDGE,"E8");var subQ4=sQuery(id+"F0.wireOp",EDGE,"E7.1.0");var subQ5=makeQuery(id+"F3.opExtrude","CAP_FACE",FACE,{"disambiguationData":[OSD([sQuery(id+"F2.wireOp",EDGE,"E17"),sQuery(id+"F2.wireOp",EDGE,"E18")])],"isStart":true});var subQ6=sQuery(id+"F0.wireOp",EDGE,"E7.2.1");var subQ7=makeQuery(id+"F1.opExtrude","CAP_FACE",FACE,{"disambiguationData":[OSD([sQuery(id+"F0.wireOp",EDGE,"E0"),sQuery(id+"F0.wireOp",EDGE,"E2"),subQ4,sQuery(id+"F0.wireOp",EDGE,"E7.1.1"),sQuery(id+"F0.wireOp",EDGE,"E7.2.0"),subQ6,sQuery(id+"F0.wireOp",EDGE,"E7.3.0"),sQuery(id+"F0.wireOp",EDGE,"E7.3.1"),subQ3,sQuery(id+"F0.wireOp",EDGE,"E9"),sQuery(id+"F0.wireOp",EDGE,"E10"),sQuery(id+"F0.wireOp",EDGE,"E13"),sQuery(id+"F0.wireOp",EDGE,"E14"),sQuery(id+"F0.wireOp",EDGE,"E15"),sQuery(id+"F0.wireOp",EDGE,"E16.1.0"),sQuery(id+"F0.wireOp",EDGE,"E16.1.2"),sQuery(id+"F0.wireOp",EDGE,"E16.1.3"),sQuery(id+"F0.wireOp",EDGE,"E16.2.0"),sQuery(id+"F0.wireOp",EDGE,"E16.2.2"),sQuery(id+"F0.wireOp",EDGE,"E16.2.3"),sQuery(id+"F0.wireOp",EDGE,"E16.3.0"),sQuery(id+"F0.wireOp",EDGE,"E16.3.2"),sQuery(id+"F0.wireOp",EDGE,"E16.3.3")])],"isStart":true});Q0=makeQuery(id+"F15.boolean.opBoolean","SPLIT",EDGE,{"disambiguationData":[TD([subQ7,subQ5,subQ2,subQ1,makeQuery(id+"F7.opExtrude","SWEPT_FACE",FACE,{"disambiguationData":[OSD([sQuery(id+"F6.wireOp",EDGE,"E27")])]}),makeQuery(id+"F10.opFillet","BLEND_FACE",FACE,{"disambiguationData":[OSD([subQ4,subQ3])]}),makeQuery(id+"F15.opExtrude","SWEPT_FACE",FACE,{"disambiguationData":[OSD([sQuery(id+"F14.wireOp",EDGE,"E41.2.1")])]})])],"derivedFrom":makeQuery(id+"F5.boolean.opBoolean","SPLIT",EDGE,{"disambiguationData":[topologyDisambiguationEdgeConnected([subQ2,subQ1]),TD([makeQuery(id+"F1.opExtrude","SWEPT_FACE",FACE,{"disambiguationData":[OSD([subQ4])]})])],"derivedFrom":makeQuery(id+"F5.opExtrude","CAP_EDGE",EDGE,{"disambiguationData":[OSD([subQ0])],"isStart":true})})});}
            var Q1;
            {var subQ0=sQuery(id+"F4.wireOp",EDGE,"E20");var subQ1=makeQuery(id+"F5.opExtrude","SWEPT_FACE",FACE,{"disambiguationData":[OSD([subQ0])]});var subQ2=sQuery(id+"F0.wireOp",EDGE,"E8");var subQ3=sQuery(id+"F0.wireOp",EDGE,"E7.2.0");var subQ4=makeQuery(id+"F5.opExtrude","CAP_FACE",FACE,{"disambiguationData":[OSD([sQuery(id+"F4.wireOp",EDGE,"E19"),subQ0])],"isStart":true});var subQ5=makeQuery(id+"F3.opExtrude","CAP_FACE",FACE,{"disambiguationData":[OSD([sQuery(id+"F2.wireOp",EDGE,"E17"),sQuery(id+"F2.wireOp",EDGE,"E18")])],"isStart":true});var subQ6=sQuery(id+"F0.wireOp",EDGE,"E7.3.1");var subQ7=makeQuery(id+"F1.opExtrude","CAP_FACE",FACE,{"disambiguationData":[OSD([sQuery(id+"F0.wireOp",EDGE,"E0"),sQuery(id+"F0.wireOp",EDGE,"E2"),sQuery(id+"F0.wireOp",EDGE,"E7.1.0"),sQuery(id+"F0.wireOp",EDGE,"E7.1.1"),subQ3,sQuery(id+"F0.wireOp",EDGE,"E7.2.1"),sQuery(id+"F0.wireOp",EDGE,"E7.3.0"),subQ6,subQ2,sQuery(id+"F0.wireOp",EDGE,"E9"),sQuery(id+"F0.wireOp",EDGE,"E10"),sQuery(id+"F0.wireOp",EDGE,"E13"),sQuery(id+"F0.wireOp",EDGE,"E14"),sQuery(id+"F0.wireOp",EDGE,"E15"),sQuery(id+"F0.wireOp",EDGE,"E16.1.0"),sQuery(id+"F0.wireOp",EDGE,"E16.1.2"),sQuery(id+"F0.wireOp",EDGE,"E16.1.3"),sQuery(id+"F0.wireOp",EDGE,"E16.2.0"),sQuery(id+"F0.wireOp",EDGE,"E16.2.2"),sQuery(id+"F0.wireOp",EDGE,"E16.2.3"),sQuery(id+"F0.wireOp",EDGE,"E16.3.0"),sQuery(id+"F0.wireOp",EDGE,"E16.3.2"),sQuery(id+"F0.wireOp",EDGE,"E16.3.3")])],"isStart":true});Q1=makeQuery(id+"F15.boolean.opBoolean","SPLIT",EDGE,{"disambiguationData":[TD([subQ7,subQ5,subQ4,subQ1,makeQuery(id+"F7.opExtrude","SWEPT_FACE",FACE,{"disambiguationData":[OSD([sQuery(id+"F6.wireOp",EDGE,"E31.1.3.0")])]}),makeQuery(id+"F10.opFillet","BLEND_FACE",FACE,{"disambiguationData":[OSD([subQ3,subQ2])]}),makeQuery(id+"F15.opExtrude","SWEPT_FACE",FACE,{"disambiguationData":[OSD([sQuery(id+"F14.wireOp",EDGE,"E41.3.1")])]})])],"derivedFrom":makeQuery(id+"F5.boolean.opBoolean","SPLIT",EDGE,{"disambiguationData":[topologyDisambiguationEdgeConnected([subQ4,subQ1]),TD([makeQuery(id+"F1.opExtrude","SWEPT_FACE",FACE,{"disambiguationData":[OSD([subQ3])]})])],"derivedFrom":makeQuery(id+"F5.opExtrude","CAP_EDGE",EDGE,{"disambiguationData":[OSD([subQ0])],"isStart":true})})});}
            var Q2;
            {var subQ0=sQuery(id+"F4.wireOp",EDGE,"E20");var subQ1=makeQuery(id+"F5.opExtrude","SWEPT_FACE",FACE,{"disambiguationData":[OSD([subQ0])]});var subQ2=makeQuery(id+"F5.opExtrude","CAP_FACE",FACE,{"disambiguationData":[OSD([sQuery(id+"F4.wireOp",EDGE,"E19"),subQ0])],"isStart":true});var subQ3=makeQuery(id+"F3.opExtrude","CAP_FACE",FACE,{"disambiguationData":[OSD([sQuery(id+"F2.wireOp",EDGE,"E17"),sQuery(id+"F2.wireOp",EDGE,"E18")])],"isStart":true});var subQ4=sQuery(id+"F0.wireOp",EDGE,"E9");var subQ5=sQuery(id+"F0.wireOp",EDGE,"E8");var subQ6=sQuery(id+"F0.wireOp",EDGE,"E7.3.0");var subQ7=makeQuery(id+"F1.opExtrude","CAP_FACE",FACE,{"disambiguationData":[OSD([sQuery(id+"F0.wireOp",EDGE,"E0"),sQuery(id+"F0.wireOp",EDGE,"E2"),sQuery(id+"F0.wireOp",EDGE,"E7.1.0"),sQuery(id+"F0.wireOp",EDGE,"E7.1.1"),sQuery(id+"F0.wireOp",EDGE,"E7.2.0"),sQuery(id+"F0.wireOp",EDGE,"E7.2.1"),subQ6,sQuery(id+"F0.wireOp",EDGE,"E7.3.1"),subQ5,subQ4,sQuery(id+"F0.wireOp",EDGE,"E10"),sQuery(id+"F0.wireOp",EDGE,"E13"),sQuery(id+"F0.wireOp",EDGE,"E14"),sQuery(id+"F0.wireOp",EDGE,"E15"),sQuery(id+"F0.wireOp",EDGE,"E16.1.0"),sQuery(id+"F0.wireOp",EDGE,"E16.1.2"),sQuery(id+"F0.wireOp",EDGE,"E16.1.3"),sQuery(id+"F0.wireOp",EDGE,"E16.2.0"),sQuery(id+"F0.wireOp",EDGE,"E16.2.2"),sQuery(id+"F0.wireOp",EDGE,"E16.2.3"),sQuery(id+"F0.wireOp",EDGE,"E16.3.0"),sQuery(id+"F0.wireOp",EDGE,"E16.3.2"),sQuery(id+"F0.wireOp",EDGE,"E16.3.3")])],"isStart":true});Q2=makeQuery(id+"F15.boolean.opBoolean","SPLIT",EDGE,{"disambiguationData":[TD([subQ7,subQ3,subQ2,subQ1,makeQuery(id+"F7.opExtrude","SWEPT_FACE",FACE,{"disambiguationData":[OSD([sQuery(id+"F6.wireOp",EDGE,"E30.2.0")])]}),makeQuery(id+"F10.opFillet","BLEND_FACE",FACE,{"disambiguationData":[OSD([subQ6,subQ5])]}),makeQuery(id+"F15.opExtrude","SWEPT_FACE",FACE,{"disambiguationData":[OSD([sQuery(id+"F14.wireOp",EDGE,"E38")])]})])],"derivedFrom":makeQuery(id+"F5.boolean.opBoolean","SPLIT",EDGE,{"disambiguationData":[topologyDisambiguationEdgeConnected([subQ2,subQ1]),TD([makeQuery(id+"F1.opExtrude","SWEPT_FACE",FACE,{"disambiguationData":[OSD([subQ6])]})])],"derivedFrom":makeQuery(id+"F5.opExtrude","CAP_EDGE",EDGE,{"disambiguationData":[OSD([subQ0])],"isStart":true})})});}
            var Q3;
            {var subQ0=sQuery(id+"F4.wireOp",EDGE,"E20");var subQ1=makeQuery(id+"F5.opExtrude","SWEPT_FACE",FACE,{"disambiguationData":[OSD([subQ0])]});var subQ2=makeQuery(id+"F5.opExtrude","CAP_FACE",FACE,{"disambiguationData":[OSD([sQuery(id+"F4.wireOp",EDGE,"E19"),subQ0])],"isStart":true});var subQ3=makeQuery(id+"F3.opExtrude","CAP_FACE",FACE,{"disambiguationData":[OSD([sQuery(id+"F2.wireOp",EDGE,"E17"),sQuery(id+"F2.wireOp",EDGE,"E18")])],"isStart":true});var subQ4=sQuery(id+"F0.wireOp",EDGE,"E10");var subQ5=sQuery(id+"F0.wireOp",EDGE,"E8");var subQ6=sQuery(id+"F0.wireOp",EDGE,"E7.1.1");var subQ7=makeQuery(id+"F1.opExtrude","CAP_FACE",FACE,{"disambiguationData":[OSD([sQuery(id+"F0.wireOp",EDGE,"E0"),sQuery(id+"F0.wireOp",EDGE,"E2"),sQuery(id+"F0.wireOp",EDGE,"E7.1.0"),subQ6,sQuery(id+"F0.wireOp",EDGE,"E7.2.0"),sQuery(id+"F0.wireOp",EDGE,"E7.2.1"),sQuery(id+"F0.wireOp",EDGE,"E7.3.0"),sQuery(id+"F0.wireOp",EDGE,"E7.3.1"),subQ5,sQuery(id+"F0.wireOp",EDGE,"E9"),subQ4,sQuery(id+"F0.wireOp",EDGE,"E13"),sQuery(id+"F0.wireOp",EDGE,"E14"),sQuery(id+"F0.wireOp",EDGE,"E15"),sQuery(id+"F0.wireOp",EDGE,"E16.1.0"),sQuery(id+"F0.wireOp",EDGE,"E16.1.2"),sQuery(id+"F0.wireOp",EDGE,"E16.1.3"),sQuery(id+"F0.wireOp",EDGE,"E16.2.0"),sQuery(id+"F0.wireOp",EDGE,"E16.2.2"),sQuery(id+"F0.wireOp",EDGE,"E16.2.3"),sQuery(id+"F0.wireOp",EDGE,"E16.3.0"),sQuery(id+"F0.wireOp",EDGE,"E16.3.2"),sQuery(id+"F0.wireOp",EDGE,"E16.3.3")])],"isStart":true});Q3=makeQuery(id+"F15.boolean.opBoolean","SPLIT",EDGE,{"disambiguationData":[TD([subQ7,subQ3,subQ2,subQ1,makeQuery(id+"F7.opExtrude","SWEPT_FACE",FACE,{"disambiguationData":[OSD([sQuery(id+"F6.wireOp",EDGE,"E30.1.0")])]}),makeQuery(id+"F10.opFillet","BLEND_FACE",FACE,{"disambiguationData":[OSD([sQuery(id+"F0.wireOp",EDGE,"E4"),subQ5,subQ4])]}),makeQuery(id+"F15.opExtrude","SWEPT_FACE",FACE,{"disambiguationData":[OSD([sQuery(id+"F14.wireOp",EDGE,"E41.1.1")])]})])],"derivedFrom":makeQuery(id+"F5.boolean.opBoolean","SPLIT",EDGE,{"disambiguationData":[topologyDisambiguationEdgeConnected([subQ2,subQ1]),TD([makeQuery(id+"F1.opExtrude","SWEPT_FACE",FACE,{"disambiguationData":[OSD([subQ6])]})])],"derivedFrom":makeQuery(id+"F5.opExtrude","CAP_EDGE",EDGE,{"disambiguationData":[OSD([subQ0])],"isStart":true})})});}
            chamfer(context, id + "F16", {"entities" : qUnion([Q0, Q1, Q2, Q3]), "width" : 5.15 * mm, "tangentPropagation" : true});
        }
    });
